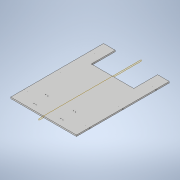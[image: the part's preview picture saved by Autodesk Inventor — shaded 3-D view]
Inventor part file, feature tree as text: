
AUTODESK INVENTOR PART (.ipt)
format: ipt  version: 2021 (Build 250183000, 183)  size: 186,368 bytes
history: native  units: in
note: dims shown in document units (in); Inventor stores cm internally (conversion verified against a paired STEP export)
features: sketch x7, extrude x6, other x1, hole x1, plane x1, mirror x1
ambient origin geometry x8: Origin, YZ Plane, XZ Plane, XY Plane, X Axis, Y Axis, Z Axis, Center Point
bodies: Solid1 (feature_tree)
feature tree (17):
  other  "main plate"
  extrude  "Extrusion1"  Depth=17.5in
  extrude  "Extrusion2"  Depth=0.25in
  extrude  "Extrusion3"  Depth=3.746in
  extrude  "Extrusion4"  Depth=1.185in
  extrude  "Extrusion5"  Depth=0.107in
  hole  "Hole1"  [1 undecoded]
  plane  "Work Plane1"
  mirror  "Mirror1"
  extrude  "Extrusion6"  Depth=2.2in
  sketch  "Sketch1"  dims[d0=12.4in d1=17.5in]
  sketch  "Sketch2"  dims[d2=0.25in d3=0.0in d4=0.107in]
  sketch  "Sketch3"  dims[d5=0.107in d7=3.746in]
  sketch  "Sketch4"  dims[d8=0.394in d9=1.185in]
  sketch  "Sketch5"  dims[d10=1.0in d11=0.0in d12=0.107in]
  sketch  "Sketch6"  dims[d13=0.107in d14=2.482in]
  sketch  "Sketch7"  dims[d15=2.482in d16=0.394in d17=3.846in d18=1.0in d19=0.0in d20=0.107in d21=0.107in d22=0.394in d23=2.929in d24=3.665in d25=1.0in d26=0.0in d27=0.107in d28=0.107in d31=1.13in d32=0.394in d34=1.0in d35=0.0in d36=8.741in d37=1.185in d38=1.13in d39=0.25in d40=0.125in d41=0.125in d42=0.125in d43=2.5in d44=2.5in d45=12.5in d46=6.25in d47=0.196in d48=0.5in d49=0.375in d50=0.25in d51=0.5635in d52=0.75in d53=0.8108in d54=8.0in d55=4.5in d56=2.2in d57=0.0in d58=0.0in]
note: 1 required parameter value undecoded (feature->parameter linkage not recoverable at this tier; creation-order binding heuristic only, values carry confidence <= 0.55)
